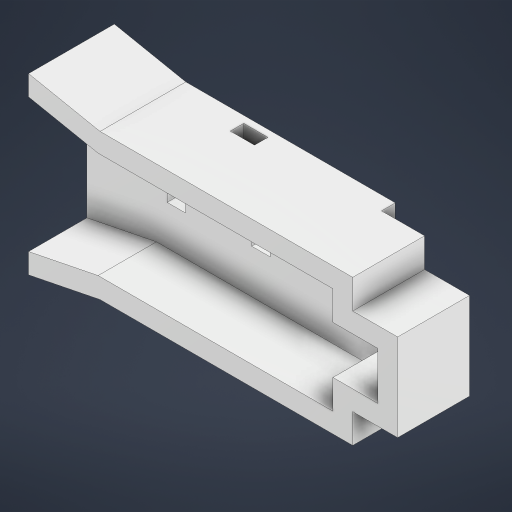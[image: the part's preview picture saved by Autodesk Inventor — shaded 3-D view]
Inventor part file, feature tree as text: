
AUTODESK INVENTOR PART (.ipt)
format: ipt  version: 2024.1 (Build 281209000, 209)  size: 4,430,336 bytes
history: native  units: mm
features: extrude x8, sketch x8, projected_geometry x7, plane x3, other x2
ambient origin geometry x8: Origin, YZ Plane, XZ Plane, XY Plane, X Axis, Y Axis, Z Axis, Center Point
bodies: Solid1 (feature_tree)
feature tree (28):
  other  "3D_PCB1_2024-08-12"
  plane  "Work Plane1"
  extrude  "Extrusion1"  Depth=14.696mm
  sketch  "Sketch3"  dims[d2=10.0mm d3=10.0mm]
  plane  "Work Plane2"
  extrude  "Extrusion2"  Depth=10.0mm
  extrude  "Extrusion3"  Depth=3.0mm
  extrude  "Extrusion4"  Depth=3.0mm
  extrude  "Extrusion5"  Depth=2.76mm TaperAngle=0.0deg
  plane  "Work Plane3"
  extrude  "Extrusion6"  Depth=13.0mm
  extrude  "Extrusion7"  Depth=14.939mm
  extrude  "Extrusion8"  Depth=6.0mm
  sketch  "Sketch2"  dims[d0=4.1mm d1=14.696mm]
  sketch  "Sketch4"  dims[d4=10.0mm d5=3.0mm]
  sketch  "Sketch5"  dims[d6=3.0mm d7=3.0mm]
  sketch  "Sketch6"  dims[d8=0.0mm d9=2.76mm d10=0.0mm]
  projected_geometry  "Projected Loop1"
  projected_geometry  "Projected Loop2"
  sketch  "Sketch7"  dims[d11=0.0mm d12=3.328mm d13=0.0mm d14=13.0mm]
  sketch  "Sketch8"  dims[d15=47.5mm d16=14.939mm]
  projected_geometry  "Projected Loop3"
  sketch  "Sketch10"  dims[d17=3.0mm d18=5.0mm d19=10.0mm d20=10.0mm d21=5.0mm d22=0.3mm d23=5.0mm d24=0.3mm d25=13.0mm d26=0.0mm d28=3.0mm d29=0.0mm d30=0.0mm d31=0.0mm d32=5.4mm d33=3.0mm d34=0.0mm d35=3.0mm d36=0.0mm d45=6.0mm d46=0.0mm d47=0.0mm]
  projected_geometry  "Projected Loop4"
  other  "3D_PCB1_2024-08-12.obj"
  projected_geometry  "Project Cut Edges1"
  projected_geometry  "Project Cut Edges2"
  projected_geometry  "Project Cut Edges3"
